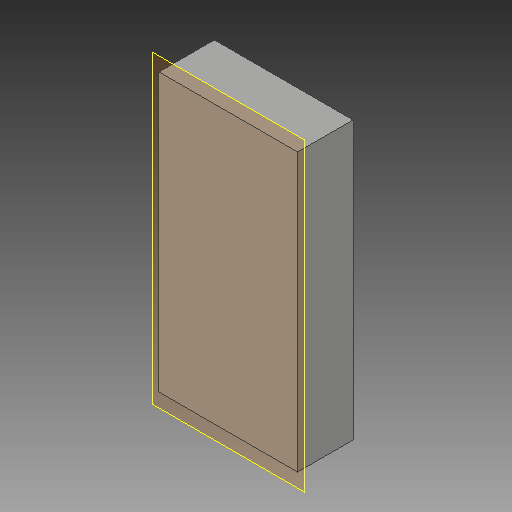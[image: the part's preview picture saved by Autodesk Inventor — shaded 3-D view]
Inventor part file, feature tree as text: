
AUTODESK INVENTOR PART (.ipt)
format: ipt  version: 2018 (Build 220112000, 112)  size: 92,160 bytes
history: native  units: mm
features: other x3, sketch x2, plane x1, extrude x1, hole x1, projected_geometry x1
ambient origin geometry x8: Origin, YZ Plane, XZ Plane, XY Plane, X Axis, Y Axis, Z Axis, Center Point
bodies: Solid1 (feature_tree)
feature tree (9):
  plane  "Work Plane1"
  extrude  "Extrusion1"  Depth=20.0mm
  hole  "Hole1"  [1 undecoded]
  sketch  "Sketch1"  dims[d0=10.0mm d1=20.0mm]
  sketch  "Sketch2"  dims[d2=4.0mm d3=0.0mm d4=5.0mm d5=6.0mm d6=8.0mm d7=2.0mm d8=90.0deg d9=8.0mm d10=20.594885mm]
  projected_geometry  "Projected Loop1"
  parser-record x1  (decoder bookkeeping rows leaked as tree rows — omitted from the tree; the rows remain in map.json)
  other  "håndfang.iam"
  other  "stang:2"
note: 1 required parameter value undecoded (feature->parameter linkage not recoverable at this tier; creation-order binding heuristic only, values carry confidence <= 0.55)
note: 1 file-system path scrubbed to <path> (originals preserved in map.json)
